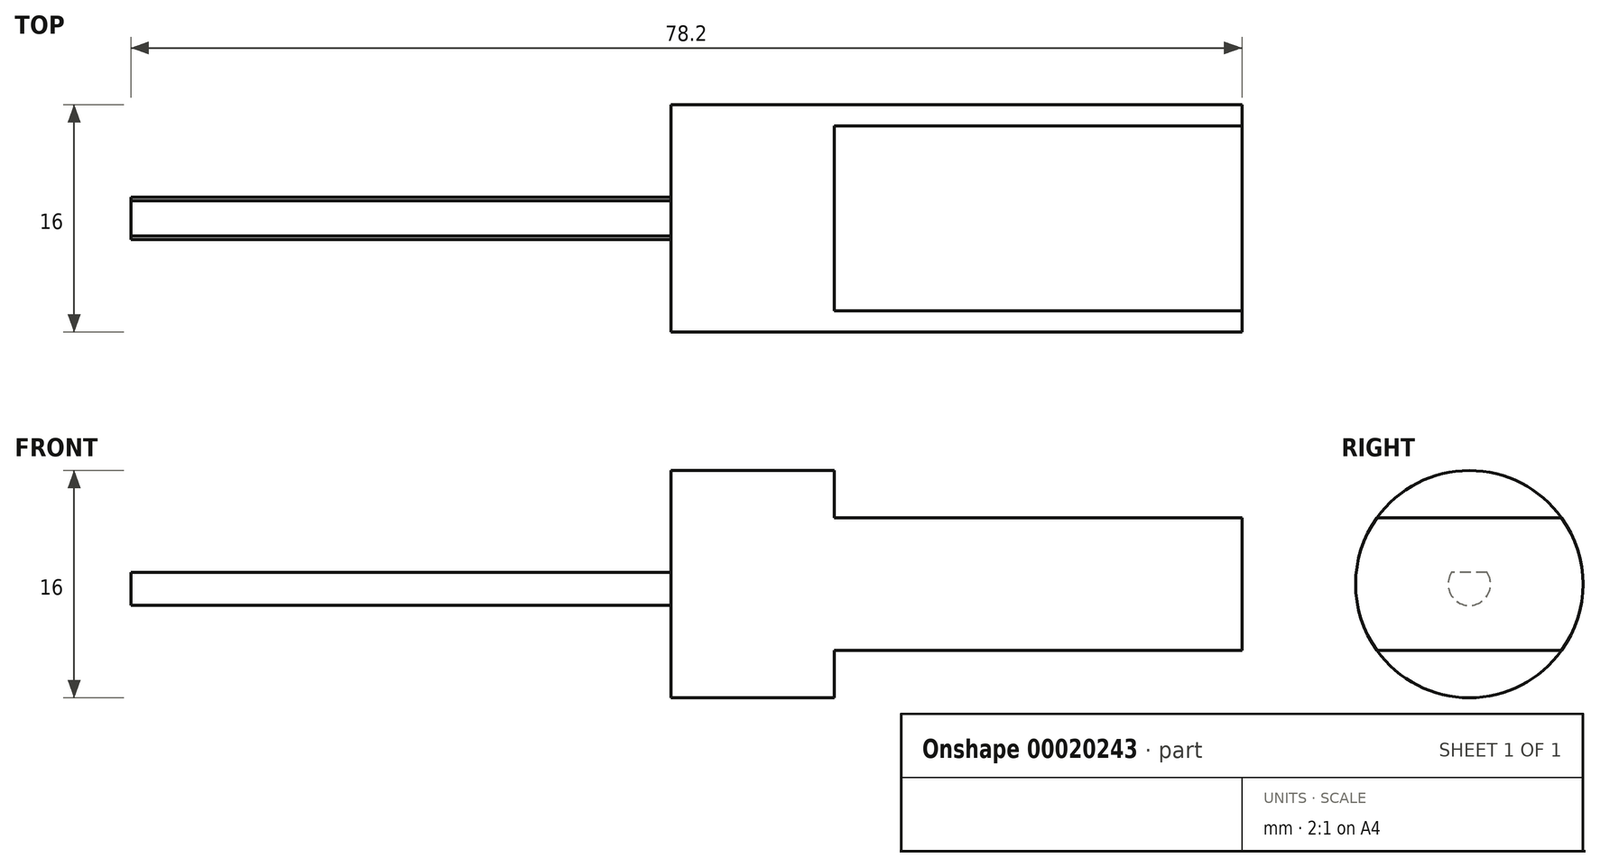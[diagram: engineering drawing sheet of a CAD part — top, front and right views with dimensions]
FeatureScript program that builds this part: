
annotation { "Feature Type Name" : "Feature", "Feature Type Description" : "" }
export const myFeature = defineFeature(function(context is Context, id is Id, definition is map)
    precondition{}
    {
        {
            var Q0;
            Q0=qCreatedBy(makeId("Right.planeOp"),FACE);
            var sketch = newSketch(context, id + "F0", { "sketchPlane" : qUnion([Q0])});
            skCircle(sketch, "E0", {"center": v(0, 0) * mm, "radius": 8 * mm});
            skSolve(sketch);
        }
        {
            var Q0;
            Q0 = qSketchRegion(id + "F0", true);
            extrude(context, id + "F1", {"entities" : qUnion([Q0]), "depth" : 11.5 * mm});
        }
        {
            var Q0;
            Q0=makeQuery(id+"F1.opExtrude","CAP_FACE",FACE,{"disambiguationData":[OSD([sQuery(id+"F0.wireOp",EDGE,"E0")])],"isStart":false});
            var sketch = newSketch(context, id + "F2", { "sketchPlane" : qUnion([Q0])});
            skCircle(sketch, "E1", {"center": v(0, 0) * mm, "radius": 8 * mm});
            skSolve(sketch);
        }
        {
            var Q0;
            Q0 = qSketchRegion(id + "F2", true);
            extrude(context, id + "F3", {"entities" : qUnion([Q0]), "operationType" : NewBodyOperationType.ADD, "depth" : 28.7 * mm});
        }
        {
            var Q0;
            Q0=makeQuery(id+"F3.opExtrude","CAP_FACE",FACE,{"disambiguationData":[OSD([sQuery(id+"F2.wireOp",EDGE,"E1")])],"isStart":false});
            var sketch = newSketch(context, id + "F4", { "sketchPlane" : qUnion([Q0])});
            skCircle(sketch, "E2", {"center": v(0, 0) * mm, "radius": 8 * mm, "construction": true});
            skLineSegment(sketch, "E3.rect.bottom", {"start": v(6.5, 4.66) * mm, "end": v(-6.5, 4.66) * mm});
            skLineSegment(sketch, "E3.rect.top", {"start": v(6.5, -4.66) * mm, "end": v(-6.5, -4.66) * mm});
            skLineSegment(sketch, "E3.rect.left", {"start": v(6.5, 4.66) * mm, "end": v(6.5, -4.66) * mm});
            skLineSegment(sketch, "E3.rect.right", {"start": v(-6.5, 4.66) * mm, "end": v(-6.5, -4.66) * mm});
            skSolve(sketch);
        }
        {
            var Q0;
            {var subQ1=sQuery(id+"F4.wireOp",EDGE,"E3.rect.bottom");Q0=makeQuery(id+"F4.imprint","IMPRINT",FACE,{"disambiguationData":[TD([[makeQuery(id+"F4.imprint","IMPRINT",EDGE,{"derivedFrom":subQ1}),-1.0]])]});}
            var Q1;
            {var subQ1=sQuery(id+"F4.wireOp",EDGE,"E3.rect.top");Q1=makeQuery(id+"F4.imprint","IMPRINT",FACE,{"disambiguationData":[TD([[makeQuery(id+"F4.imprint","IMPRINT",EDGE,{"derivedFrom":subQ1}),1.0]])]});}
            extrude(context, id + "F5", {"entities" : qUnion([Q0, Q1]), "operationType" : NewBodyOperationType.REMOVE, "oppositeDirection" : true, "depth" : 28.7 * mm});
        }
        {
            var Q0;
            Q0=makeQuery(id+"F1.opExtrude","CAP_FACE",FACE,{"disambiguationData":[OSD([sQuery(id+"F0.wireOp",EDGE,"E0")])],"isStart":true});
            var sketch = newSketch(context, id + "F6", { "sketchPlane" : qUnion([Q0])});
            skCircle(sketch, "E4", {"center": v(0, 0) * mm, "radius": 1.5 * mm});
            skSolve(sketch);
        }
        {
            var Q0;
            Q0 = qSketchRegion(id + "F6", true);
            extrude(context, id + "F7", {"entities" : qUnion([Q0]), "operationType" : NewBodyOperationType.ADD, "depth" : 38 * mm});
        }
        {
            var Q0;
            Q0=makeQuery(id+"F7.opExtrude","CAP_FACE",FACE,{"disambiguationData":[OSD([sQuery(id+"F6.wireOp",EDGE,"E4")])],"isStart":false});
            var sketch = newSketch(context, id + "F8", { "sketchPlane" : qUnion([Q0])});
            skCircle(sketch, "E5", {"center": v(0, 0) * mm, "radius": 1.5 * mm, "construction": true});
            skLineSegment(sketch, "E6.rect.bottom", {"start": v(-1.25, 0.83) * mm, "end": v(1.25, 0.83) * mm, "construction": true});
            skLineSegment(sketch, "E6.rect.top", {"start": v(-1.25, -0.83) * mm, "end": v(1.25, -0.83) * mm, "construction": true});
            skLineSegment(sketch, "E6.rect.left", {"start": v(-1.25, 0.83) * mm, "end": v(-1.25, -0.83) * mm, "construction": true});
            skLineSegment(sketch, "E6.rect.right", {"start": v(1.25, 0.83) * mm, "end": v(1.25, -0.83) * mm, "construction": true});
            skLineSegment(sketch, "E7", {"start": v(-1.25, 0.83) * mm, "end": v(1.25, 0.83) * mm});
            skSolve(sketch);
        }
        {
            var Q0;
            {var subQ1=sQuery(id+"F8.wireOp",EDGE,"E7");Q0=makeQuery(id+"F8.imprint","IMPRINT",FACE,{"disambiguationData":[TD([[makeQuery(id+"F8.imprint","IMPRINT",EDGE,{"derivedFrom":subQ1}),1.0]])]});}
            extrude(context, id + "F9", {"entities" : qUnion([Q0]), "operationType" : NewBodyOperationType.REMOVE, "oppositeDirection" : true, "depth" : 38 * mm});
        }
    });
